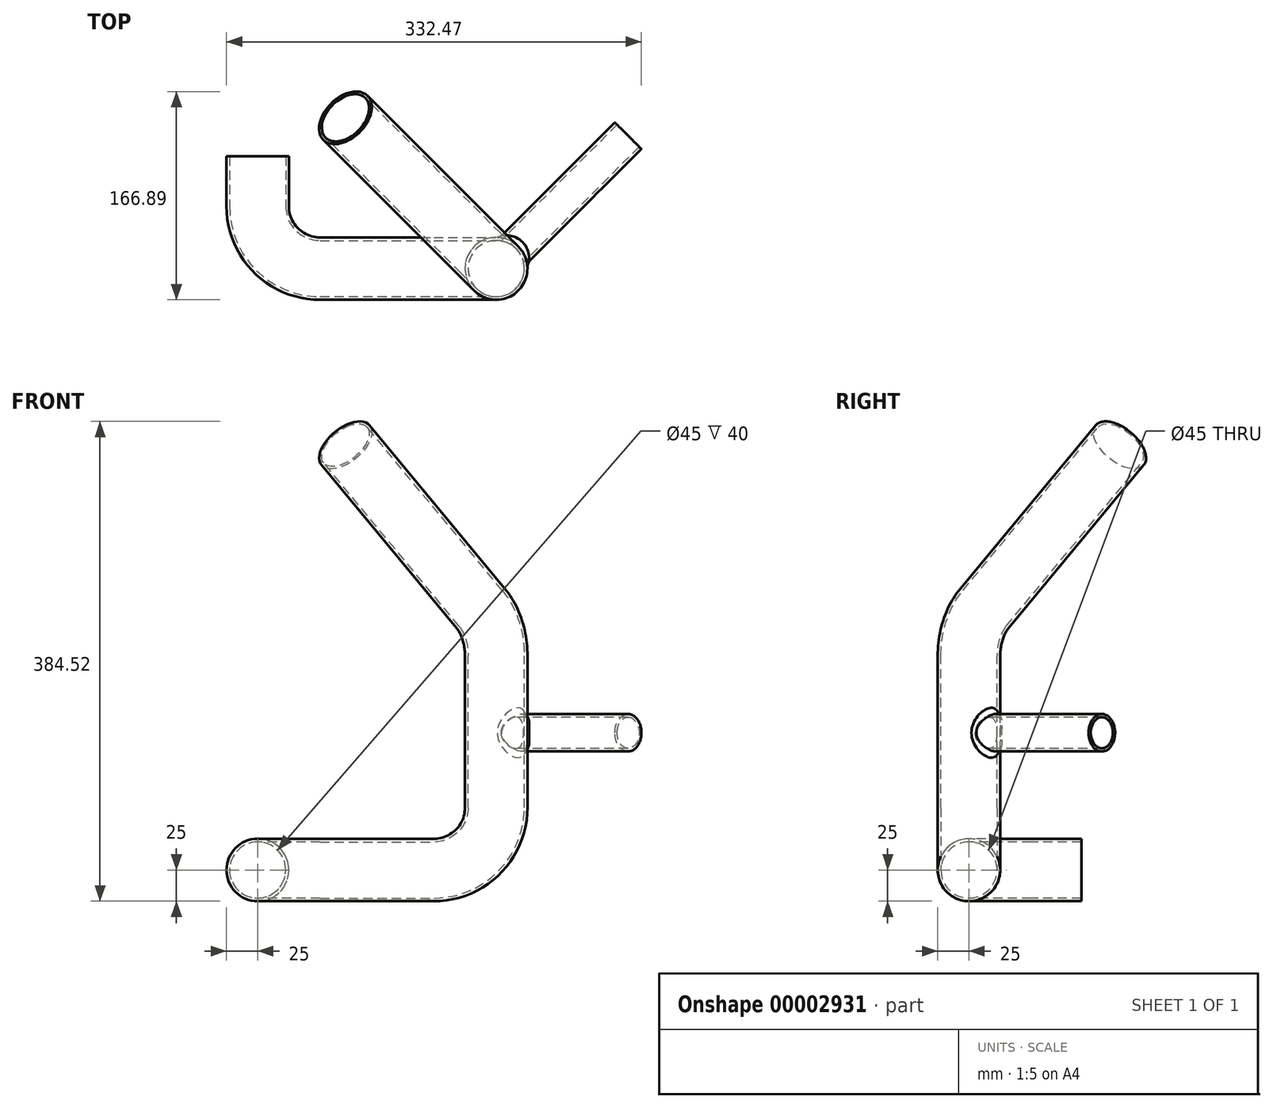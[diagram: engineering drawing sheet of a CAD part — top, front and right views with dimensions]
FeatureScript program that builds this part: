
annotation { "Feature Type Name" : "Feature", "Feature Type Description" : "" }
export const myFeature = defineFeature(function(context is Context, id is Id, definition is map)
    precondition{}
    {
        {
            var Q0;
            Q0=qCreatedBy(makeId("Front.planeOp"),FACE);
            var sketch = newSketch(context, id + "F0", { "sketchPlane" : qUnion([Q0])});
            skCircle(sketch, "E0", {"center": v(-40, 30) * mm, "radius": 25 * mm});
            skSolve(sketch);
        }
        {
            var Q0;
            Q0=sQuery(id+"F0.wireOp",VERTEX,"E0.center");
            var Q1;
            Q1=qCreatedBy(makeId("Top.planeOp"),FACE);
            cPlane(context, id + "F1", {"entities" : qUnion([Q0, Q1]), "cplaneType" : CPlaneType.PLANE_POINT, "offset" : 150 * mm, "width" : 150 * mm, "height" : 150 * mm});
        }
        {
            var Q0;
            Q0=qCreatedBy(id+"F1.planeOp",FACE);
            var sketch = newSketch(context, id + "F2", { "sketchPlane" : qUnion([Q0])});
            skLineSegment(sketch, "E1", {"start": v(-40, 0) * mm, "end": v(-40, -40) * mm});
            skLineSegment(sketch, "E2", {"start": v(10, -90) * mm, "end": v(60, -90) * mm});
            skPoint(sketch, "E3.visualSharp", {"position": v(-40, -90) * mm});
            skArc(sketch, "E3.filletArc", {"start": v(-40, -40) * mm, "mid": v(-25.36, -75.36) * mm, "end": v(10, -90) * mm});
            skSolve(sketch);
        }
        {
            var Q0;
            Q0=sQuery(id+"F2.wireOp",VERTEX,"E3.filletArc.end");
            var Q1;
            Q1=qCreatedBy(makeId("Front.planeOp"),FACE);
            cPlane(context, id + "F3", {"entities" : qUnion([Q0, Q1]), "cplaneType" : CPlaneType.PLANE_POINT, "offset" : 150 * mm, "width" : 150 * mm, "height" : 150 * mm});
        }
        {
            var Q0;
            Q0=qCreatedBy(id+"F3.planeOp",FACE);
            var sketch = newSketch(context, id + "F4", { "sketchPlane" : qUnion([Q0])});
            skLineSegment(sketch, "E4", {"start": v(60, 30) * mm, "end": v(101.17, 30) * mm});
            skLineSegment(sketch, "E5", {"start": v(151.17, 80) * mm, "end": v(151.17, 150) * mm});
            skPoint(sketch, "E6.visualSharp", {"position": v(151.17, 30) * mm});
            skArc(sketch, "E6.filletArc", {"start": v(101.17, 30) * mm, "mid": v(136.53, 44.64) * mm, "end": v(151.17, 80) * mm});
            skSolve(sketch);
        }
        {
            var Q0;
            Q0=sQuery(id+"F4.wireOp",EDGE,"E5");
            cPlane(context, id + "F5", {"entities" : qUnion([Q0]), "cplaneType" : CPlaneType.LINE_ANGLE, "offset" : 150 * mm, "angle" : 45 * degree, "width" : 150 * mm, "height" : 150 * mm});
        }
        {
            var Q0;
            Q0=qCreatedBy(id+"F5.planeOp",FACE);
            var sketch = newSketch(context, id + "F6", { "sketchPlane" : qUnion([Q0])});
            skLineSegment(sketch, "E7", {"start": v(-170.53, 150) * mm, "end": v(-170.53, 201.66) * mm});
            skLineSegment(sketch, "E8", {"start": v(-152.99, 239.7) * mm, "end": v(0.33, 370.5) * mm});
            skPoint(sketch, "E9.visualSharp", {"position": v(-170.53, 224.72) * mm});
            skArc(sketch, "E9.filletArc", {"start": v(-152.99, 239.7) * mm, "mid": v(-165.94, 222.6) * mm, "end": v(-170.53, 201.66) * mm});
            skSolve(sketch);
        }
        {
            var Q0;
            Q0=makeQuery(id+"F0.imprint","IMPRINT",FACE,{"disambiguationData":[TD([[makeQuery(id+"F0.imprint","IMPRINT",EDGE,{"derivedFrom":sQuery(id+"F0.wireOp",EDGE,"E0")}),1.0]])]});
            var Q1;
            Q1=sQuery(id+"F2.wireOp",EDGE,"E1");
            var Q2;
            Q2=sQuery(id+"F2.wireOp",EDGE,"E3.filletArc");
            var Q3;
            Q3=sQuery(id+"F2.wireOp",EDGE,"E2");
            var Q4;
            Q4=sQuery(id+"F4.wireOp",EDGE,"E4");
            var Q5;
            Q5=sQuery(id+"F4.wireOp",EDGE,"E6.filletArc");
            var Q6;
            Q6=sQuery(id+"F4.wireOp",EDGE,"E5");
            var Q7;
            Q7=sQuery(id+"F6.wireOp",EDGE,"E7");
            var Q8;
            Q8=sQuery(id+"F6.wireOp",EDGE,"E9.filletArc");
            var Q9;
            Q9=sQuery(id+"F6.wireOp",EDGE,"E8");
            sweep(context, id + "F7", {"profiles" : qUnion([Q0]), "path" : qUnion([Q1, Q2, Q3, Q4, Q5, Q6, Q7, Q8, Q9])});
        }
        {
            var Q0;
            Q0=qCreatedBy(id+"F5.planeOp",FACE);
            var sketch = newSketch(context, id + "F8", { "sketchPlane" : qUnion([Q0])});
            skCircle(sketch, "E10", {"center": v(-170, 140) * mm, "radius": 15 * mm});
            skSolve(sketch);
        }
        {
            var Q0;
            Q0 = qSketchRegion(id + "F8", true);
            var Q1;
            Q1=makeQuery(id+"F7.opSweep","SWEPT_FACE",FACE,{"disambiguationData":[OSD([sQuery(id+"F0.wireOp",EDGE,"E0"),sQuery(id+"F4.wireOp",EDGE,"E5")])]});
            extrude(context, id + "F9", {"entities" : qUnion([Q0]), "operationType" : NewBodyOperationType.ADD, "endBoundEntity" : qUnion([Q1]), "depth" : 150 * mm});
        }
        {
            var Q0;
            Q0=makeQuery(id+"F7.opSweep","CAP_FACE",FACE,{"disambiguationData":[OSD([sQuery(id+"F0.wireOp",EDGE,"E0"),sQuery(id+"F6.wireOp",VERTEX,"E8.end")])],"isStart":false});
            var Q1;
            Q1=makeQuery(id+"F7.opSweep","CAP_FACE",FACE,{"disambiguationData":[OSD([sQuery(id+"F0.wireOp",EDGE,"E0"),sQuery(id+"F2.wireOp",VERTEX,"E1.start")])],"isStart":true});
            var Q2;
            Q2=makeQuery(id+"F9.opExtrude","CAP_FACE",FACE,{"disambiguationData":[OSD([sQuery(id+"F8.wireOp",EDGE,"E10")])],"isStart":false});
            shell(context, id + "F10", {"entities" : qUnion([Q0, Q1, Q2]), "thickness" : 2.5 * mm});
        }
        {
            var Q0;
            Q0=makeQuery(id+"F9.boolean.opBoolean","INTERSECT",EDGE,{"derivedFrom":[makeQuery(id+"F7.opSweep","SWEPT_FACE",FACE,{"disambiguationData":[OSD([sQuery(id+"F0.wireOp",EDGE,"E0"),sQuery(id+"F4.wireOp",EDGE,"E5")])]}),makeQuery(id+"F9.opExtrude","SWEPT_FACE",FACE,{"disambiguationData":[OSD([sQuery(id+"F8.wireOp",EDGE,"E10")])]})]});
            chamfer(context, id + "F11", {"entities" : qUnion([Q0]), "width" : 5 * mm});
        }
    });
